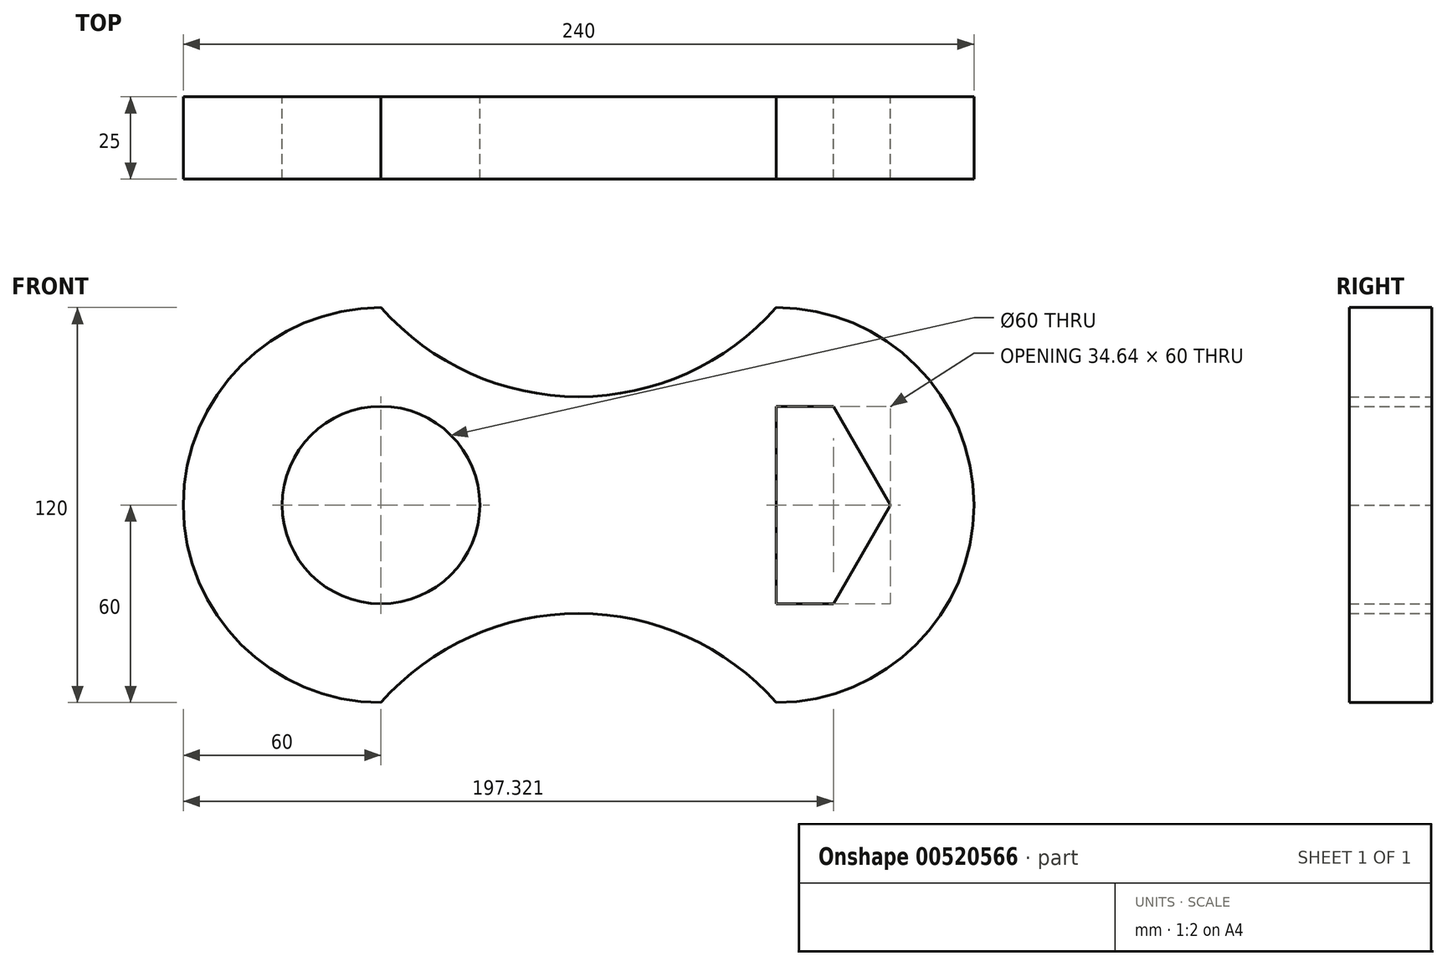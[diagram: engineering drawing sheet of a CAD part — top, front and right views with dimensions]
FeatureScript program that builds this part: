
annotation { "Feature Type Name" : "Feature", "Feature Type Description" : "" }
export const myFeature = defineFeature(function(context is Context, id is Id, definition is map)
    precondition{}
    {
        {
            var Q0;
            Q0=qCreatedBy(makeId("Front.planeOp"),FACE);
            var sketch = newSketch(context, id + "F0", { "sketchPlane" : qUnion([Q0])});
            skCircle(sketch, "E0", {"center": v(0, 0) * mm, "radius": 30 * mm});
            skArc(sketch, "E1", {"start": v(0, 60) * mm, "mid": v(-60, 0) * mm, "end": v(0, -60) * mm});
            skLineSegment(sketch, "E2", {"start": v(120, 0) * mm, "end": v(120, 30) * mm});
            skLineSegment(sketch, "E3", {"start": v(120, 0) * mm, "end": v(120, -60) * mm});
            skArc(sketch, "E4", {"start": v(120, -60) * mm, "mid": v(60, -32.92) * mm, "end": v(0, -60) * mm});
            skArc(sketch, "E5", {"start": v(0, 60) * mm, "mid": v(60, 32.92) * mm, "end": v(120, 60) * mm});
            skArc(sketch, "E6.trimOffspring", {"start": v(120, -60) * mm, "mid": v(180, 0) * mm, "end": v(120, 60) * mm});
            skCircle(sketch, "E7.cCircle", {"center": v(120, 0) * mm, "radius": 30 * mm, "construction": true});
            skLineSegment(sketch, "E7.0", {"start": v(102.68, 30) * mm, "end": v(137.32, 30) * mm});
            skLineSegment(sketch, "E7.1", {"start": v(137.32, 30) * mm, "end": v(154.64, 0) * mm});
            skLineSegment(sketch, "E7.2", {"start": v(154.64, 0) * mm, "end": v(137.32, -30) * mm});
            skLineSegment(sketch, "E7.3", {"start": v(137.32, -30) * mm, "end": v(102.68, -30) * mm});
            skLineSegment(sketch, "E7.4", {"start": v(102.68, -30) * mm, "end": v(85.36, 0) * mm});
            skLineSegment(sketch, "E7.5", {"start": v(85.36, 0) * mm, "end": v(102.68, 30) * mm});
            skPoint(sketch, "E7.0.midPoint", {"position": v(120, 30) * mm});
            skSolve(sketch);
        }
        {
            var Q0;
            {var subQ1=sQuery(id+"F0.wireOp",EDGE,"E2");Q0=makeQuery(id+"F0.imprint","IMPRINT",FACE,{"disambiguationData":[TD([[makeQuery(id+"F0.imprint","IMPRINT",EDGE,{"derivedFrom":subQ1}),1.0]])]});}
            var Q1;
            Q1=makeQuery(id+"F0.imprint","IMPRINT",FACE,{"disambiguationData":[TD([[makeQuery(id+"F0.imprint","IMPRINT",EDGE,{"derivedFrom":sQuery(id+"F0.wireOp",EDGE,"E0")}),-1.0]])]});
            extrude(context, id + "F1", {"entities" : qUnion([Q0, Q1]), "depth" : 25 * mm, "offsetDistance" : 25 * mm});
        }
    });
